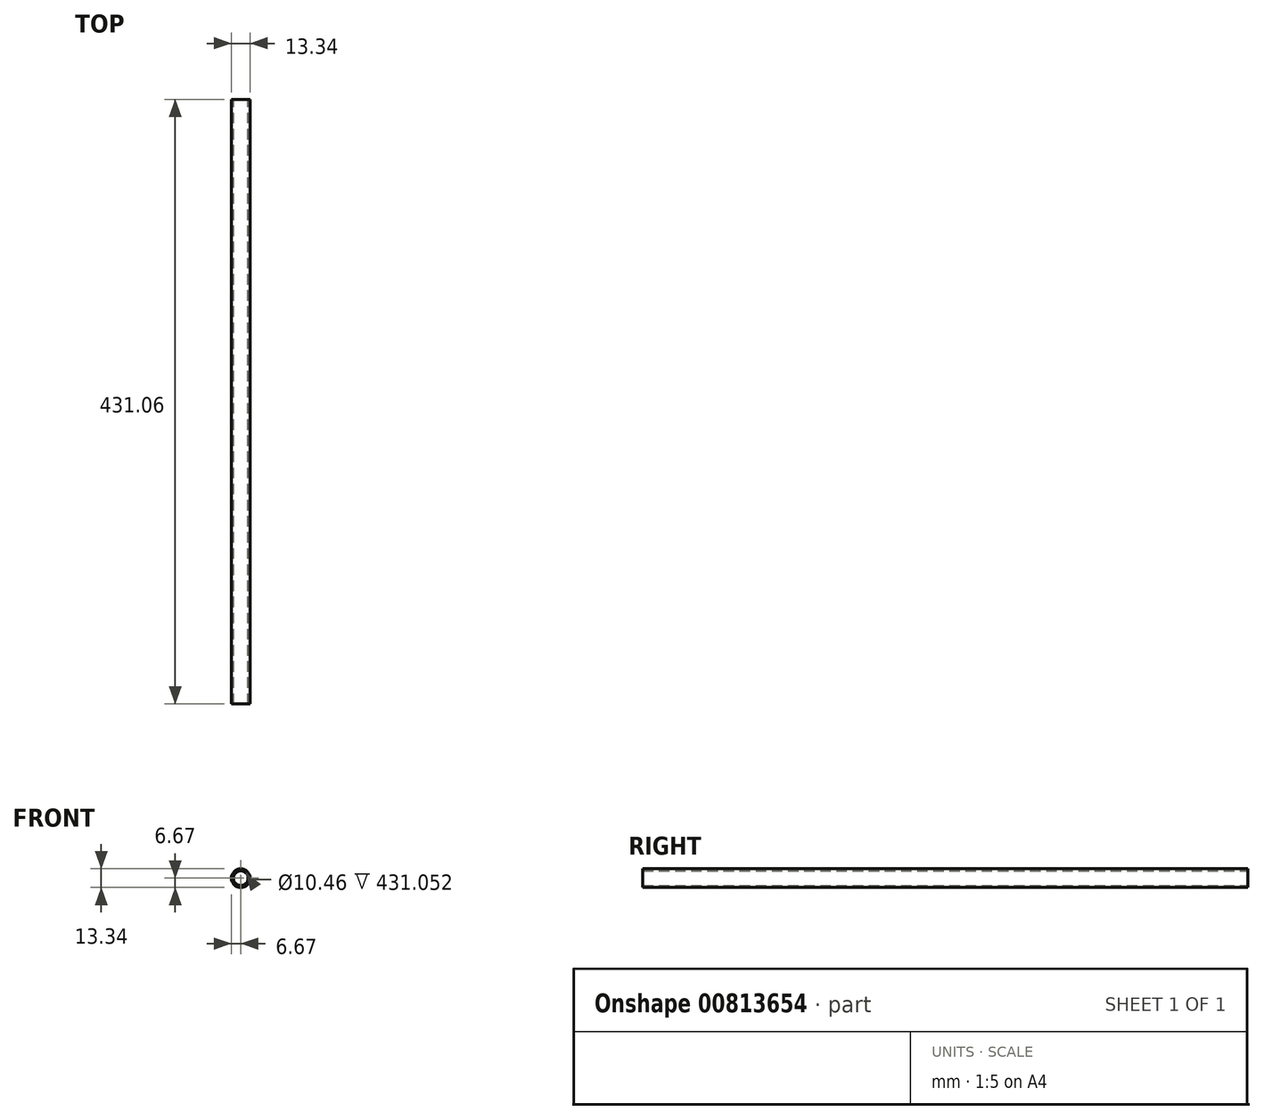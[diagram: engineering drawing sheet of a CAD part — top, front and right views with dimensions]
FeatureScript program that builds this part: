
annotation { "Feature Type Name" : "Feature", "Feature Type Description" : "" }
export const myFeature = defineFeature(function(context is Context, id is Id, definition is map)
    precondition{}
    {
        {
            var Q0;
            Q0=qCreatedBy(makeId("Front.planeOp"),FACE);
            var sketch = newSketch(context, id + "F0", { "sketchPlane" : qUnion([Q0])});
            skCircle(sketch, "E0", {"center": v(0, 0) * mm, "radius": 6.67 * mm});
            skCircle(sketch, "E1", {"center": v(0, 0) * mm, "radius": 5.23 * mm});
            skSolve(sketch);
        }
        {
            var Q0;
            Q0 = qSketchRegion(id + "F0", true);
            extrude(context, id + "F1", {"entities" : qUnion([Q0]), "endBound" : BoundingType.SYMMETRIC, "depth" : 431.05 * mm, "offsetDistance" : 25.4 * mm});
        }
    });
